# Revit family: Shower-Shower_Column_Kit-KOHLER-Atom-K-32878T_1
name_source: partatom
category: Plumbing Fixtures
units: mm (PartAtom-declared; Revit-internal decimal feet)

## family parameters
Cut with Voids When Loaded = No
Host = Face
OmniClass Number = 23.31.17.00
OmniClass Title = Showers
Part Type = Normal
Room Calculation Point = No
Round Connector Dimension = Use Diameter
Shared = No

## types (1)
- CP-Polished Chrome
    ADA Compliant = No
    Assembly Code = D2010700
    CW Connection = Yes
    Cold Water Inlet = Cold Water Inlet
    Date Modified = 04/14/2023
    Default Elevation = 36"
    Description = 3 Way Shower Column Lever SF Handshower
    Drain Included = No
    Finish = Kohler-Metal-CP-Polished_Chrome
    Flow Rate = 8 GPM
    HW Connection = Yes
    Handle Clearance = 3"
    Height = 51 13/16"
    Hot Water Inlet = Hot Water Inlet
    Length = 21 5/16"
    Manufacturer = Kohler Co.
    Master Format 2014 = 22 42 23
    Master Format 2014 Name = Residential Showers
    Material = Premium Metal Construction
    Model = K-32878T-4-CP
    Pressure = 43.50 psi
    Product Name = Atom
    Spout Reach = 6 1/8"
    Type = 1
    URL = http://www.kohler.com.cn
    Vent Connection = No
    Waste Connection = No
    Waste Water Outlet = Waste Water Outlet
    WaterSense Certified = No
    Width = 5 15/16"

## geometry (parser evidence)
native form markers: Sweep x6
no freeform markers — native parametric forms only
